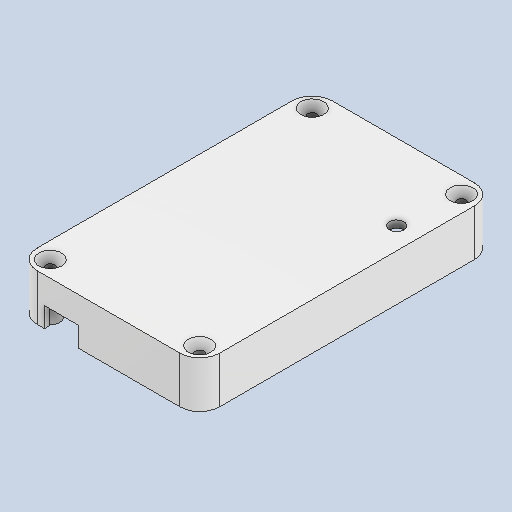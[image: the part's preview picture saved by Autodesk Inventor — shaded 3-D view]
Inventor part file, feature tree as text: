
AUTODESK INVENTOR PART (.ipt)
format: ipt  version: 2022 (Build 260153000, 153)  size: 213,504 bytes
history: native  units: mm
features: sketch x10, extrude x6, hole x4, other x1
ambient origin geometry x8: Origin, YZ Plane, XZ Plane, XY Plane, X Axis, Y Axis, Z Axis, Center Point
bodies: Body1 (feature_tree)
feature tree (21):
  other  "Твердое тело1"
  extrude  "Выдавливание1"  Depth=5.0mm
  extrude  "Выдавливание2"  Depth=5.0mm
  extrude  "Выдавливание4"  Depth=5.0mm
  extrude  "Выдавливание5"  Depth=5.0mm TaperAngle=0.0deg
  extrude  "Выдавливание6"  Depth=2.0mm TaperAngle=0.0deg
  extrude  "Выдавливание7"  Depth=10.911mm TaperAngle=0.0deg
  hole  "Отверстие1"  [1 undecoded]
  hole  "Отверстие2"  [1 undecoded]
  hole  "Отверстие3"  [1 undecoded]
  hole  "Отверстие4"  [1 undecoded]
  sketch  "Эскиз1"
  sketch  "Эскиз2"
  sketch  "Эскиз4"
  sketch  "Эскиз5"
  sketch  "Эскиз6"
  sketch  "Эскиз7"
  sketch  "Эскиз8"
  sketch  "Эскиз9"
  sketch  "Эскиз10"
  sketch  "Эскиз11"
note: 4 required parameter values undecoded (feature->parameter linkage not recoverable at this tier; creation-order binding heuristic only, values carry confidence <= 0.55)
